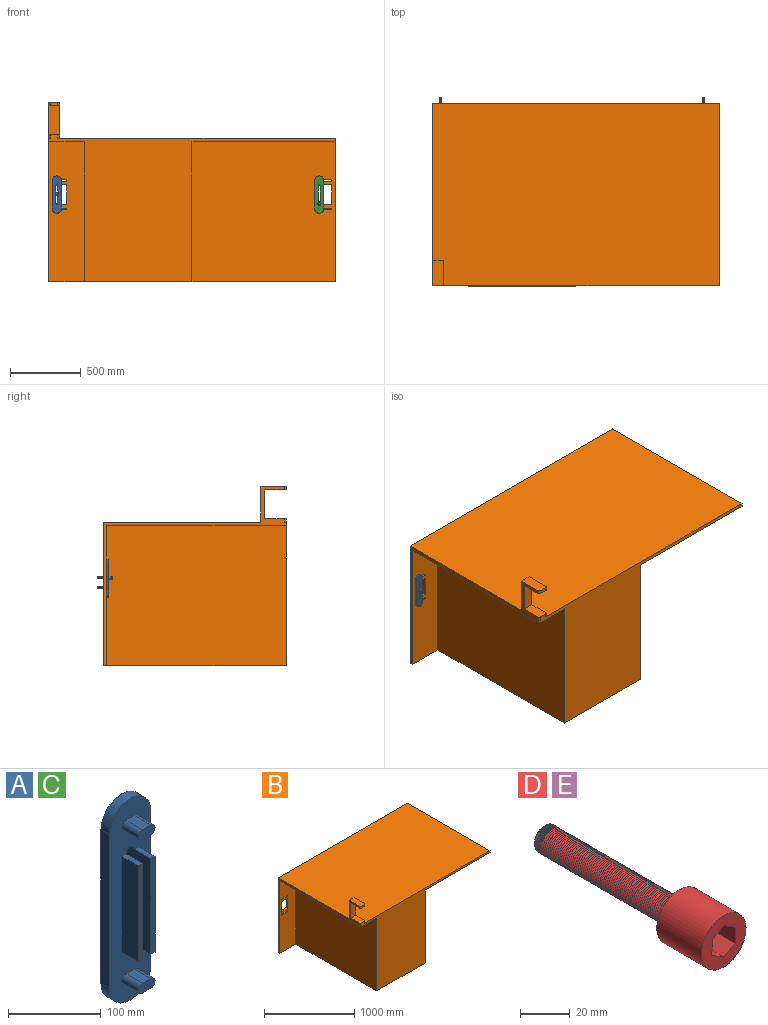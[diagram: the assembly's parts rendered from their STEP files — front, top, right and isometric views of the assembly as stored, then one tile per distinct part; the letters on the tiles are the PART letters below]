
ASSEMBLY  parts=5 mates=4
PART A: 28 faces, bbox 63.5x38.1x266.7 mm
  f0: cylinder r=6.35mm len=25.4mm, axis (0,1,0), area 506.7mm2, adj f1,f3,f4,f19
  f1: plane 25.4x12.7mm, normal (0,0,1), area 322.6mm2, adj f0,f2,f4,f19
  f2: cylinder r=6.35mm len=25.4mm, axis (0,1,0), area 506.7mm2, adj f1,f3,f4,f19
  f3: plane 25.4x12.7mm, normal (0,0,-1), area 322.6mm2, adj f0,f2,f4,f19
  f4: plane 25.4x12.7mm, normal (0,-1,0), area 288mm2, adj f0,f1,f2,f3
  f5: cylinder r=6.35mm len=25.4mm, axis (0,1,0), area 506.7mm2, adj f6,f8,f9,f19
  f6: plane 25.4x12.7mm, normal (0,0,1), area 322.6mm2, adj f5,f7,f9,f19
  f7: cylinder r=6.35mm len=25.4mm, axis (0,1,0), area 506.7mm2, adj f6,f8,f9,f19
  f8: plane 25.4x12.7mm, normal (0,0,-1), area 322.6mm2, adj f5,f7,f9,f19
  f9: plane 25.4x12.7mm, normal (0,-1,0), area 288mm2, adj f5,f6,f7,f8
  f10: plane 203.2x12.7mm, normal (-1,0,0), area 2580.6mm2, adj f11,f17,f18,f19
  f11: cylinder r=31.75mm len=63.5mm, axis (0,-1,0), area 1266.8mm2, adj f10,f12,f18,f19
  f12: plane 203.2x12.7mm, normal (1,0,0), area 2580.6mm2, adj f11,f17,f18,f19
  f13: plane 127x38.1mm, normal (-1,0,0), area 4838.7mm2, adj f14,f16,f18,f20,f21,f23
  f14: cylinder r=6.35mm len=12.7mm, axis (0,-1,0), area 253.4mm2, adj f13,f15,f18,f19
  f15: plane 127x38.1mm, normal (1,0,0), area 4838.7mm2, adj f14,f16,f18,f24,f26,f27
  f16: cylinder r=6.35mm len=12.7mm, axis (0,-1,0), area 253.4mm2, adj f13,f15,f18,f19
  f17: cylinder r=31.75mm len=63.5mm, axis (0,-1,0), area 1266.8mm2, adj f10,f12,f18,f19
  f18: plane 266.7x63.5mm, normal (0,1,0), area 14330.5mm2, adj f10,f11,f12,f13,f14,f15,f16,f17
  f19: plane 266.7x63.5mm, normal (0,-1,0), area 12141.7mm2, adj f0,f1,f2,f3,f5,f6,f7,f8
  f20: plane 25.4x6.35mm, normal (0,0,1), area 161.3mm2, adj f13,f19,f22,f23
  f21: plane 25.4x6.35mm, normal (0,0,-1), area 161.3mm2, adj f13,f19,f22,f23
  f22: plane 127x25.4mm, normal (1,0,0), area 3225.8mm2, adj f19,f20,f21,f23
  f23: plane 127x6.35mm, normal (0,-1,0), area 806.4mm2, adj f13,f20,f21,f22
  f24: plane 25.4x6.35mm, normal (0,0,1), area 161.3mm2, adj f15,f19,f25,f27
  f25: plane 127x25.4mm, normal (-1,0,0), area 3225.8mm2, adj f19,f24,f26,f27
  f26: plane 25.4x6.35mm, normal (0,0,-1), area 161.3mm2, adj f15,f19,f25,f27
  f27: plane 127x6.35mm, normal (0,-1,0), area 806.5mm2, adj f15,f24,f25,f26
PART B: 56 faces, bbox 2032x1295.4x1270 mm
  f0: plane 2032x1041.4mm, normal (0,-1,0), area 807740.3mm2, adj f1,f5,f8,f9,f11,f12,f14,f47
  f1: plane 1295.4x1270mm, normal (-1,0,0), area 71612.8mm2, adj f0,f2,f5,f7,f10,f11,f12,f48
  f2: cylinder r=12.7mm len=25.4mm, axis (0,0,-1), area 506.7mm2, adj f1,f13,f52,f53
  f3: cylinder r=12.7mm len=25.4mm, axis (0,0,-1), area 506.7mm2, adj f4,f13,f52,f53
  f4: plane 254x165.1mm, normal (1,0,0), area 13548.4mm2, adj f3,f5,f50,f51,f52,f53,f54,f55
  f5: plane 2032x1295.4mm, normal (0,0,1), area 2618739.1mm2, adj f0,f1,f4,f10,f14,f50,f51
  f6: plane 1016x990.6mm, normal (0,-1,0), area 989779.3mm2, adj f9,f12,f14,f31,f32,f33,f34,f35
  f7: plane 990.6x254mm, normal (0,-1,0), area 234942.1mm2, adj f1,f8,f12,f15,f16,f17,f18,f19
  f8: plane 1270x990.6mm, normal (-1,0,0), area 1258062mm2, adj f0,f7,f12,f48
  f9: plane 1270x990.6mm, normal (1,0,0), area 1258062mm2, adj f0,f6,f12,f47
  f10: plane 2032x1016mm, normal (0,1,0), area 2031171.4mm2, adj f1,f5,f12,f14,f15,f16,f17,f18
  f11: plane 12.7x12.7mm, normal (0,0,1), area 34.6mm2, adj f0,f1,f49
  f12: plane 2032x1295.4mm, normal (0,0,-1), area 1019352.8mm2, adj f0,f1,f6,f7,f8,f9,f10,f14
  f13: plane 50.8x25.4mm, normal (0,-1,0), area 1290.3mm2, adj f2,f3,f52,f53
  f14: plane 1295.4x1016mm, normal (1,0,0), area 58064.4mm2, adj f0,f5,f6,f10,f12,f47
  f15: cylinder r=6.35mm len=25.4mm, axis (0,-1,0), area 506.7mm2, adj f7,f10,f16,f18
  f16: plane 88.9x25.4mm, normal (0,0,1), area 2258.1mm2, adj f7,f10,f15,f17
  f17: cylinder r=6.35mm len=25.4mm, axis (0,-1,0), area 506.7mm2, adj f7,f10,f16,f18
  f18: plane 88.9x25.4mm, normal (0,0,-1), area 2258.1mm2, adj f7,f10,f15,f17
  f19: cylinder r=6.35mm len=25.4mm, axis (0,-1,0), area 506.7mm2, adj f7,f10,f20,f22
  f20: plane 88.9x25.4mm, normal (0,0,1), area 2258.1mm2, adj f7,f10,f19,f21
  f21: cylinder r=6.35mm len=25.4mm, axis (0,-1,0), area 506.7mm2, adj f7,f10,f20,f22
  f22: plane 88.9x25.4mm, normal (0,0,-1), area 2258.1mm2, adj f7,f10,f19,f21
  f23: plane 127x25.4mm, normal (-1,0,0), area 3225.8mm2, adj f7,f10,f24,f30
  f24: cylinder r=6.35mm len=25.4mm, axis (0,-1,0), area 253.4mm2, adj f7,f10,f23,f25
  f25: plane 88.9x25.4mm, normal (0,0,-1), area 2258.1mm2, adj f7,f10,f24,f26
  f26: cylinder r=6.35mm len=25.4mm, axis (0,-1,0), area 253.4mm2, adj f7,f10,f25,f27
  f27: plane 127x25.4mm, normal (1,0,0), area 3225.8mm2, adj f7,f10,f26,f28
  f28: cylinder r=6.35mm len=25.4mm, axis (0,-1,0), area 253.4mm2, adj f7,f10,f27,f29
  f29: plane 88.9x25.4mm, normal (0,0,1), area 2258.1mm2, adj f7,f10,f28,f30
  f30: cylinder r=6.35mm len=25.4mm, axis (0,-1,0), area 253.4mm2, adj f7,f10,f23,f29
  f31: plane 127x25.4mm, normal (-1,0,0), area 3225.8mm2, adj f6,f10,f32,f38
  f32: cylinder r=6.35mm len=25.4mm, axis (0,-1,0), area 253.4mm2, adj f6,f10,f31,f33
  f33: plane 88.9x25.4mm, normal (0,0,-1), area 2258.1mm2, adj f6,f10,f32,f34
  f34: cylinder r=6.35mm len=25.4mm, axis (0,-1,0), area 253.4mm2, adj f6,f10,f33,f35
  f35: plane 127x25.4mm, normal (1,0,0), area 3225.8mm2, adj f6,f10,f34,f36
  f36: cylinder r=6.35mm len=25.4mm, axis (0,-1,0), area 253.4mm2, adj f6,f10,f35,f37
  f37: plane 88.9x25.4mm, normal (0,0,1), area 2258.1mm2, adj f6,f10,f36,f38
  f38: cylinder r=6.35mm len=25.4mm, axis (0,-1,0), area 253.4mm2, adj f6,f10,f31,f37
  f39: cylinder r=6.35mm len=25.4mm, axis (0,-1,0), area 506.7mm2, adj f6,f10,f40,f42
  f40: plane 88.9x25.4mm, normal (0,0,1), area 2258.1mm2, adj f6,f10,f39,f41
  f41: cylinder r=6.35mm len=25.4mm, axis (0,-1,0), area 506.7mm2, adj f6,f10,f40,f42
  f42: plane 88.9x25.4mm, normal (0,0,-1), area 2258.1mm2, adj f6,f10,f39,f41
  f43: cylinder r=6.35mm len=25.4mm, axis (0,-1,0), area 506.7mm2, adj f6,f10,f44,f46
  f44: plane 88.9x25.4mm, normal (0,0,1), area 2258.1mm2, adj f6,f10,f43,f45
  f45: cylinder r=6.35mm len=25.4mm, axis (0,-1,0), area 506.7mm2, adj f6,f10,f44,f46
  f46: plane 88.9x25.4mm, normal (0,0,-1), area 2258.1mm2, adj f6,f10,f43,f45
  f47: plane 1270x1016mm, normal (0,0,-1), area 1290320mm2, adj f0,f6,f9,f14
  f48: plane 1270x254mm, normal (0,0,-1), area 322580mm2, adj f0,f1,f7,f8
  f49: cylinder r=12.7mm len=25.4mm, axis (0,0,-1), area 506.7mm2, adj f0,f1,f11,f54
  f50: cylinder r=12.7mm len=25.4mm, axis (0,0,-1), area 506.7mm2, adj f0,f4,f5,f54
  f51: plane 254x76.2mm, normal (0,1,0), area 19354.8mm2, adj f1,f4,f5,f52
  f52: plane 177.8x76.2mm, normal (0,0,1), area 13479.1mm2, adj f1,f2,f3,f4,f13,f51
  f53: plane 152.4x76.2mm, normal (0,0,-1), area 11543.7mm2, adj f1,f2,f3,f4,f13,f55
  f54: plane 152.4x76.2mm, normal (0,0,1), area 11543.7mm2, adj f0,f1,f4,f49,f50,f55
  f55: plane 203.2x76.2mm, normal (0,-1,0), area 15483.8mm2, adj f1,f4,f53,f54
PART C: same geometry as A
PART D: 20 faces, bbox 26.1x102.9x26.1 mm
  f0: plane 25.4x25.4mm, normal (0,1,0), area 380mm2, adj f1,f3,f11
  f1: cylinder r=6.35mm len=12.7mm, axis (0,1,0), area 5.8mm2, adj f0,f12,f13
  f2: plane 25.4x25.4mm, normal (0,-1,0), area 355.9mm2, adj f3,f4,f5,f6,f7,f8,f9
  f3: cylinder r=12.7mm len=25.4mm, axis (0,1,0), area 2026.8mm2, adj f0,f2
  f4: plane 15.24x6.44mm, normal (-0.54,0,-0.84), area 116.1mm2, adj f2,f5,f9,f10
  f5: plane 15.24x6.75mm, normal (0.46,0,-0.89), area 116.1mm2, adj f2,f4,f6,f10
  f6: plane 15.24x7.61mm, normal (1,0,-0.04), area 116.1mm2, adj f2,f5,f7,f10
  f7: plane 15.24x6.44mm, normal (0.54,0,0.84), area 116.1mm2, adj f2,f6,f8,f10
  f8: plane 15.24x6.75mm, normal (-0.46,0,0.89), area 116.1mm2, adj f2,f7,f9,f10
  f9: plane 15.24x7.61mm, normal (-1,0,0.04), area 116.1mm2, adj f2,f4,f8,f10
  f10: plane 15.23x13.5mm, normal (0,-1,0), area 150.9mm2, adj f4,f5,f6,f7,f8,f9
  f11: cylinder r=6.35mm len=12.37mm, axis (0,1,0), area 3.9mm2, adj f0,f12,f13
  f12: plane 0.98x0.88mm, normal (0,0,1), area 0.4mm2, adj f1,f11,f13,f15,f16
  f13: bspline ~14.67x12.7mm, area 2.5mm2, adj f1,f11,f12,f15
  f14: plane 0.74x0.4mm, normal (0,0,-1), area 0.2mm2, adj f15,f17,f18,f19
  f15: bspline ~76.68x14.54mm, area 2813mm2, adj f12,f13,f14,f16,f18
  f16: bspline ~76.68x14.54mm, area 2788.6mm2, adj f12,f15,f17,f18
  f17: bspline ~12.7x7.33mm, area 1mm2, adj f14,f16,f18,f19
  f18: plane 13.22x12.8mm, normal (0,1,0), area 115.2mm2, adj f14,f15,f16,f17,f19
  f19: cylinder r=6.35mm len=11.11mm, axis (0,1,0), area 2.8mm2, adj f14,f17,f18
PART E: same geometry as D
PLACE A rot(axis=(1,0,0),180deg) t=(-961.89,0,684.72)mm
PLACE B at identity fixed
PLACE C rot(axis=(1,0,0),180deg) t=(897.34,0,684.72)mm
PLACE D rot(axis=(0,-1,0),90deg) t=(913.23,63.5,678.97)mm
PLACE E rot(axis=(0,-1,0),90deg) t=(-945.99,63.5,748.6)mm
MATE pin_slot D.f1 <-> C.f14  axis (0,1,0) through (901.7,-12.7,698.45)mm
MATE pin_slot E.f1 <-> A.f14  axis (0,1,0) through (-957.52,-12.7,768.08)mm
MATE pin_slot A.f7 <-> B.f19  axis (0,1,0) through (-963.87,25.4,863.55)mm
MATE pin_slot C.f7 <-> B.f43  axis (0,1,0) through (895.35,25.4,863.55)mm
